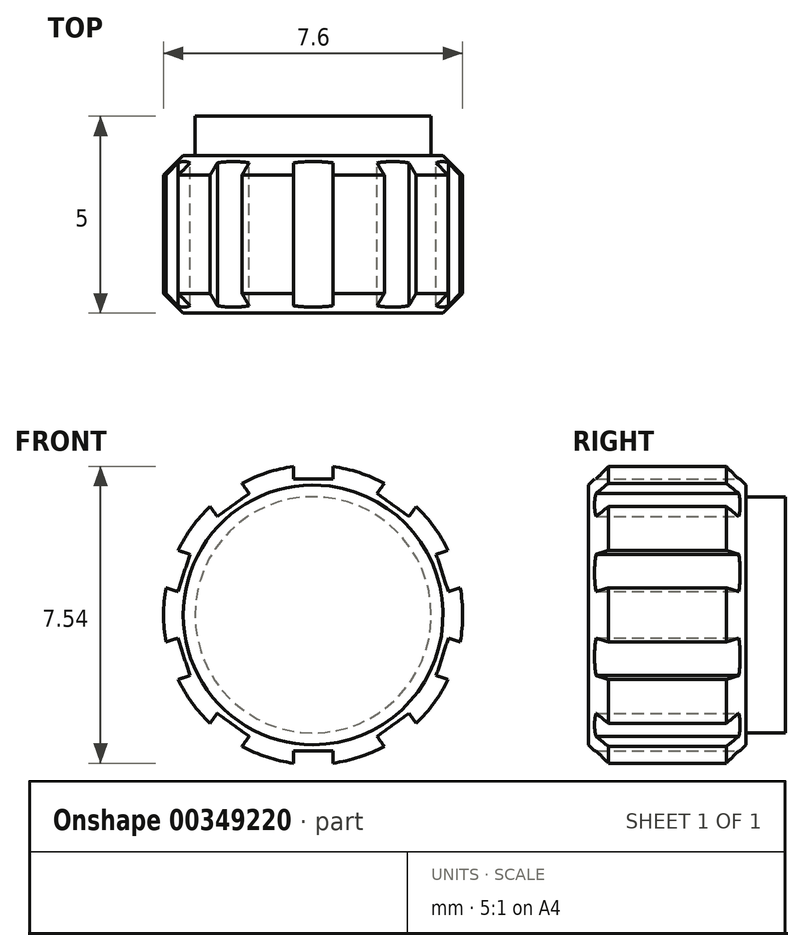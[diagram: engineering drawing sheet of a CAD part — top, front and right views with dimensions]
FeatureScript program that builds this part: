
annotation { "Feature Type Name" : "Feature", "Feature Type Description" : "" }
export const myFeature = defineFeature(function(context is Context, id is Id, definition is map)
    precondition{}
    {
        {
            var Q0;
            Q0=qCreatedBy(makeId("Front.planeOp"),FACE);
            var sketch = newSketch(context, id + "F0", { "sketchPlane" : qUnion([Q0])});
            skCircle(sketch, "E0", {"center": v(0, 0) * mm, "radius": 3.8 * mm});
            skCircle(sketch, "E1", {"center": v(0, 0) * mm, "radius": 3 * mm});
            skLineSegment(sketch, "E2", {"start": v(0, 0) * mm, "end": v(0, 3.8) * mm});
            skPoint(sketch, "E3.middle", {"position": v(0, 3.8) * mm});
            skSolve(sketch);
        }
        {
            var Q0;
            Q0=makeQuery(id+"F0.imprint","IMPRINT",FACE,{"disambiguationData":[TD([[makeQuery(id+"F0.imprint","IMPRINT",EDGE,{"derivedFrom":sQuery(id+"F0.wireOp",EDGE,"E1")}),1.0]])]});
            extrude(context, id + "F1", {"entities" : qUnion([Q0]), "oppositeDirection" : true, "depth" : 1 * mm});
        }
        {
            var Q0;
            Q0=makeQuery(id+"F0.imprint","IMPRINT",FACE,{"disambiguationData":[TD([[makeQuery(id+"F0.imprint","IMPRINT",EDGE,{"derivedFrom":sQuery(id+"F0.wireOp",EDGE,"E1")}),-1.0]])]});
            var Q1;
            Q1=makeQuery(id+"F0.imprint","IMPRINT",FACE,{"disambiguationData":[TD([[makeQuery(id+"F0.imprint","IMPRINT",EDGE,{"derivedFrom":sQuery(id+"F0.wireOp",EDGE,"E1")}),1.0]])]});
            extrude(context, id + "F2", {"entities" : qUnion([Q0, Q1]), "operationType" : NewBodyOperationType.ADD, "depth" : 4 * mm});
        }
        {
            var Q0;
            Q0=makeQuery(id+"F2.opExtrude","CAP_EDGE",EDGE,{"disambiguationData":[OSD([sQuery(id+"F0.wireOp",EDGE,"E0")])],"isStart":false});
            var Q1;
            Q1=makeQuery(id+"F2.opExtrude","CAP_EDGE",EDGE,{"disambiguationData":[OSD([sQuery(id+"F0.wireOp",EDGE,"E0")])],"isStart":true});
            chamfer(context, id + "F3", {"entities" : qUnion([Q0, Q1]), "width" : 0.5 * mm, "tangentPropagation" : true});
        }
        {
            var Q0;
            Q0=makeQuery(id+"F1.opExtrude","CAP_FACE",FACE,{"disambiguationData":[OSD([sQuery(id+"F0.wireOp",EDGE,"E1")])],"isStart":false});
            var sketch = newSketch(context, id + "F4", { "sketchPlane" : qUnion([Q0])});
            skCircle(sketch, "E4", {"center": v(0, 0) * mm, "radius": 3.8 * mm});
            skLineSegment(sketch, "E5", {"start": v(0, 0) * mm, "end": v(0, 3.8) * mm});
            skLineSegment(sketch, "E6.bottom", {"start": v(0.5, 3.45) * mm, "end": v(-0.5, 3.45) * mm});
            skLineSegment(sketch, "E6.top", {"start": v(0.5, 4.15) * mm, "end": v(-0.5, 4.15) * mm});
            skLineSegment(sketch, "E6.left", {"start": v(0.5, 3.45) * mm, "end": v(0.5, 4.15) * mm});
            skLineSegment(sketch, "E6.right", {"start": v(-0.5, 3.45) * mm, "end": v(-0.5, 4.15) * mm});
            skPoint(sketch, "E6.middle", {"position": v(0, 3.8) * mm});
            skLineSegment(sketch, "E7.1.0", {"start": v(-2.43, 2.5) * mm, "end": v(-2.84, 3.06) * mm});
            skLineSegment(sketch, "E7.1.1", {"start": v(-1.62, 3.09) * mm, "end": v(-2.43, 2.5) * mm});
            skLineSegment(sketch, "E7.1.2", {"start": v(-1.62, 3.09) * mm, "end": v(-2.03, 3.65) * mm});
            skLineSegment(sketch, "E7.2.0", {"start": v(-3.44, 0.6) * mm, "end": v(-4.1, 0.8) * mm});
            skLineSegment(sketch, "E7.2.1", {"start": v(-3.13, 1.54) * mm, "end": v(-3.44, 0.6) * mm});
            skLineSegment(sketch, "E7.2.2", {"start": v(-3.13, 1.54) * mm, "end": v(-3.8, 1.76) * mm});
            skLineSegment(sketch, "E8.1.3.0", {"start": v(-3.13, -1.54) * mm, "end": v(-3.8, -1.76) * mm});
            skLineSegment(sketch, "E8.3.3.0", {"start": v(-3.44, -0.6) * mm, "end": v(-3.13, -1.54) * mm});
            skLineSegment(sketch, "E8.6.3.0", {"start": v(-3.44, -0.6) * mm, "end": v(-4.1, -0.8) * mm});
            skLineSegment(sketch, "E8.1.4.0", {"start": v(-1.62, -3.09) * mm, "end": v(-2.03, -3.65) * mm});
            skLineSegment(sketch, "E8.3.4.0", {"start": v(-2.43, -2.5) * mm, "end": v(-1.62, -3.09) * mm});
            skLineSegment(sketch, "E8.6.4.0", {"start": v(-2.43, -2.5) * mm, "end": v(-2.84, -3.06) * mm});
            skLineSegment(sketch, "E8.1.5.0", {"start": v(0.5, -3.45) * mm, "end": v(0.5, -4.15) * mm});
            skLineSegment(sketch, "E8.3.5.0", {"start": v(-0.5, -3.45) * mm, "end": v(0.5, -3.45) * mm});
            skLineSegment(sketch, "E8.6.5.0", {"start": v(-0.5, -3.45) * mm, "end": v(-0.5, -4.15) * mm});
            skLineSegment(sketch, "E8.1.6.0", {"start": v(2.43, -2.5) * mm, "end": v(2.84, -3.06) * mm});
            skLineSegment(sketch, "E8.3.6.0", {"start": v(1.62, -3.09) * mm, "end": v(2.43, -2.5) * mm});
            skLineSegment(sketch, "E8.6.6.0", {"start": v(1.62, -3.09) * mm, "end": v(2.03, -3.65) * mm});
            skLineSegment(sketch, "E8.1.7.0", {"start": v(3.44, -0.6) * mm, "end": v(4.1, -0.8) * mm});
            skLineSegment(sketch, "E8.3.7.0", {"start": v(3.13, -1.54) * mm, "end": v(3.44, -0.6) * mm});
            skLineSegment(sketch, "E8.6.7.0", {"start": v(3.13, -1.54) * mm, "end": v(3.8, -1.76) * mm});
            skLineSegment(sketch, "E9.1.8.0", {"start": v(3.13, 1.54) * mm, "end": v(3.8, 1.76) * mm});
            skLineSegment(sketch, "E9.3.8.0", {"start": v(3.44, 0.6) * mm, "end": v(3.13, 1.54) * mm});
            skLineSegment(sketch, "E9.6.8.0", {"start": v(3.44, 0.6) * mm, "end": v(4.1, 0.8) * mm});
            skLineSegment(sketch, "E9.1.9.0", {"start": v(1.62, 3.09) * mm, "end": v(2.03, 3.65) * mm});
            skLineSegment(sketch, "E9.3.9.0", {"start": v(2.43, 2.5) * mm, "end": v(1.62, 3.09) * mm});
            skLineSegment(sketch, "E9.6.9.0", {"start": v(2.43, 2.5) * mm, "end": v(2.84, 3.06) * mm});
            skSolve(sketch);
        }
        {
            var Q0;
            {var subQ5=sQuery(id+"F4.wireOp",EDGE,"E7.1.1");Q0=makeQuery(id+"F4.imprint","IMPRINT",FACE,{"disambiguationData":[TD([[makeQuery(id+"F4.imprint","IMPRINT",EDGE,{"derivedFrom":subQ5}),-1.0]])]});}
            var Q1;
            {var subQ0=sQuery(id+"F4.wireOp",EDGE,"E5");var subQ1=sQuery(id+"F4.wireOp",EDGE,"E4");var subQ2=makeQuery(id+"F4.imprint","INTERSECT",VERTEX,{"derivedFrom":[subQ1,subQ0]});Q1=makeQuery(id+"F4.imprint","IMPRINT",FACE,{"disambiguationData":[TD([[makeQuery(id+"F4.imprint","IMPRINT",EDGE,{"disambiguationData":[TD([[subQ2,-1.0]])],"derivedFrom":subQ1}),1.0]])]});}
            var Q2;
            {var subQ0=sQuery(id+"F4.wireOp",EDGE,"E5");var subQ1=sQuery(id+"F4.wireOp",EDGE,"E4");var subQ2=makeQuery(id+"F4.imprint","INTERSECT",VERTEX,{"derivedFrom":[subQ1,subQ0]});Q2=makeQuery(id+"F4.imprint","IMPRINT",FACE,{"disambiguationData":[TD([[makeQuery(id+"F4.imprint","IMPRINT",EDGE,{"disambiguationData":[TD([[subQ2,1.0]])],"derivedFrom":subQ1}),1.0]])]});}
            var Q3;
            {var subQ5=sQuery(id+"F4.wireOp",EDGE,"E8.3.7.0");Q3=makeQuery(id+"F4.imprint","IMPRINT",FACE,{"disambiguationData":[TD([[makeQuery(id+"F4.imprint","IMPRINT",EDGE,{"derivedFrom":subQ5}),-1.0]])]});}
            var Q4;
            {var subQ5=sQuery(id+"F4.wireOp",EDGE,"E8.3.6.0");Q4=makeQuery(id+"F4.imprint","IMPRINT",FACE,{"disambiguationData":[TD([[makeQuery(id+"F4.imprint","IMPRINT",EDGE,{"derivedFrom":subQ5}),-1.0]])]});}
            var Q5;
            {var subQ5=sQuery(id+"F4.wireOp",EDGE,"E8.3.5.0");Q5=makeQuery(id+"F4.imprint","IMPRINT",FACE,{"disambiguationData":[TD([[makeQuery(id+"F4.imprint","IMPRINT",EDGE,{"derivedFrom":subQ5}),-1.0]])]});}
            var Q6;
            {var subQ5=sQuery(id+"F4.wireOp",EDGE,"E8.3.4.0");Q6=makeQuery(id+"F4.imprint","IMPRINT",FACE,{"disambiguationData":[TD([[makeQuery(id+"F4.imprint","IMPRINT",EDGE,{"derivedFrom":subQ5}),-1.0]])]});}
            var Q7;
            {var subQ5=sQuery(id+"F4.wireOp",EDGE,"E8.3.3.0");Q7=makeQuery(id+"F4.imprint","IMPRINT",FACE,{"disambiguationData":[TD([[makeQuery(id+"F4.imprint","IMPRINT",EDGE,{"derivedFrom":subQ5}),-1.0]])]});}
            var Q8;
            {var subQ5=sQuery(id+"F4.wireOp",EDGE,"E7.2.1");Q8=makeQuery(id+"F4.imprint","IMPRINT",FACE,{"disambiguationData":[TD([[makeQuery(id+"F4.imprint","IMPRINT",EDGE,{"derivedFrom":subQ5}),-1.0]])]});}
            var Q9;
            {var subQ5=sQuery(id+"F4.wireOp",EDGE,"E9.3.8.0");Q9=makeQuery(id+"F4.imprint","IMPRINT",FACE,{"disambiguationData":[TD([[makeQuery(id+"F4.imprint","IMPRINT",EDGE,{"derivedFrom":subQ5}),-1.0]])]});}
            var Q10;
            {var subQ5=sQuery(id+"F4.wireOp",EDGE,"E9.3.9.0");Q10=makeQuery(id+"F4.imprint","IMPRINT",FACE,{"disambiguationData":[TD([[makeQuery(id+"F4.imprint","IMPRINT",EDGE,{"derivedFrom":subQ5}),-1.0]])]});}
            var Q11;
            {var subQ5=sQuery(id+"F4.wireOp",EDGE,"E9.3.10.0");Q11=makeQuery(id+"F4.imprint","IMPRINT",FACE,{"disambiguationData":[TD([[makeQuery(id+"F4.imprint","IMPRINT",EDGE,{"derivedFrom":subQ5}),-1.0]])]});}
            var Q12;
            {var subQ5=sQuery(id+"F4.wireOp",EDGE,"E9.3.11.0");Q12=makeQuery(id+"F4.imprint","IMPRINT",FACE,{"disambiguationData":[TD([[makeQuery(id+"F4.imprint","IMPRINT",EDGE,{"derivedFrom":subQ5}),-1.0]])]});}
            extrude(context, id + "F5", {"entities" : qUnion([Q0, Q1, Q2, Q3, Q4, Q5, Q6, Q7, Q8, Q9, Q10, Q11, Q12]), "operationType" : NewBodyOperationType.REMOVE, "oppositeDirection" : true, "depth" : 10 * mm});
        }
    });
